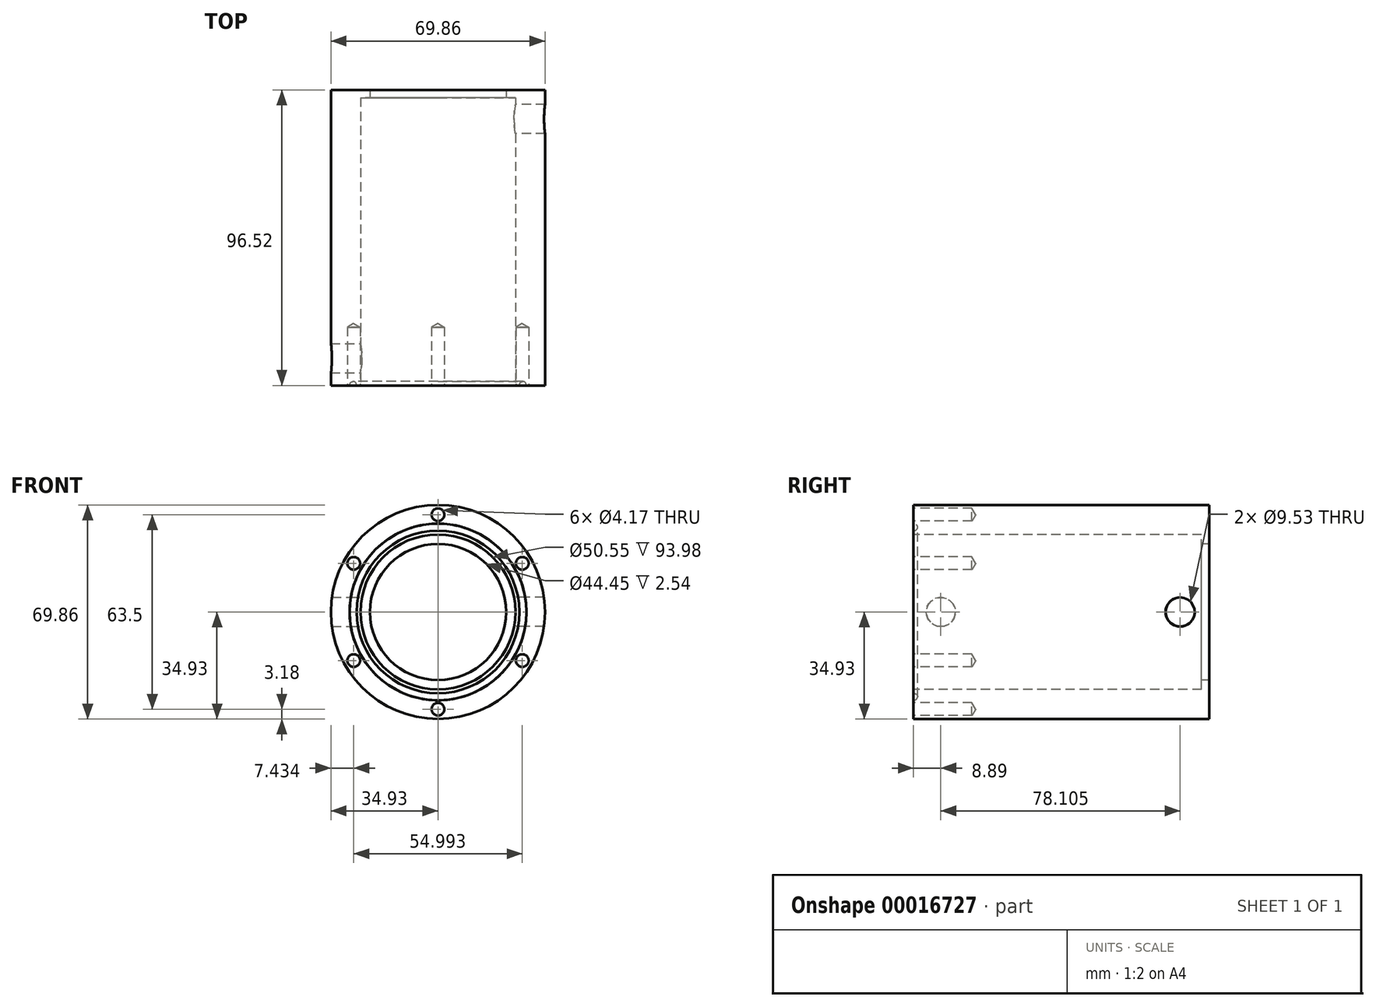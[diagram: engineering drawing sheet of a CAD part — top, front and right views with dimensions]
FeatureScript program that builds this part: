
annotation { "Feature Type Name" : "Feature", "Feature Type Description" : "" }
export const myFeature = defineFeature(function(context is Context, id is Id, definition is map)
    precondition{}
    {
        {
            var Q0;
            Q0=qCreatedBy(makeId("Front.planeOp"),FACE);
            var sketch = newSketch(context, id + "F0", { "sketchPlane" : qUnion([Q0])});
            skCircle(sketch, "E0", {"center": v(0, 0) * mm, "radius": 34.93 * mm});
            skSolve(sketch);
        }
        {
            var Q0;
            Q0=makeQuery(id+"F0.imprint","IMPRINT",FACE,{"disambiguationData":[TD([[makeQuery(id+"F0.imprint","IMPRINT",EDGE,{"derivedFrom":sQuery(id+"F0.wireOp",EDGE,"E0")}),1.0]])]});
            extrude(context, id + "F1", {"entities" : qUnion([Q0]), "oppositeDirection" : true, "depth" : 96.52 * mm});
        }
        {
            var Q0;
            Q0=qCreatedBy(makeId("Front.planeOp"),FACE);
            var sketch = newSketch(context, id + "F2", { "sketchPlane" : qUnion([Q0])});
            skPoint(sketch, "E1", {"position": v(0, 0) * mm});
            skSolve(sketch);
        }
        {
            var Q0;
            Q0=sQuery(id+"F2.wireOp",VERTEX,"E1");
            var Q1;
            Q1=makeQuery(id+"F1.opExtrude","SWEPT_BODY",BODY,{"disambiguationData":[OSD([sQuery(id+"F0.wireOp",EDGE,"E0")])]});
            hole(context, id + "F3", {"style" : HoleStyle.C_BORE, "holeDiameter" : 44.45 * mm, "cBoreDiameter" : 50.55 * mm, "cBoreDepth" : 93.98 * mm, "endStyle" : HoleEndStyle.THROUGH, "locations" : qUnion([Q0]), "scope" : qUnion([Q1])});
        }
        {
            var Q0;
            Q0=qCreatedBy(makeId("Front.planeOp"),FACE);
            var sketch = newSketch(context, id + "F4", { "sketchPlane" : qUnion([Q0])});
            skCircle(sketch, "E2", {"center": v(0, 0) * mm, "radius": 31.75 * mm});
            skPoint(sketch, "E3", {"position": v(0, 31.75) * mm});
            skPoint(sketch, "E4.1.0", {"position": v(-27.5, 15.88) * mm});
            skPoint(sketch, "E4.2.0", {"position": v(-27.5, -15.87) * mm});
            skPoint(sketch, "E4.3.0", {"position": v(0, -31.75) * mm});
            skPoint(sketch, "E4.4.0", {"position": v(27.5, -15.88) * mm});
            skPoint(sketch, "E5.0.5.0", {"position": v(27.5, 15.88) * mm});
            skSolve(sketch);
        }
        {
            var Q0;
            Q0=sQuery(id+"F4.wireOp",VERTEX,"E3");
            var Q1;
            Q1=sQuery(id+"F4.wireOp",VERTEX,"E4.4.0");
            var Q2;
            Q2=sQuery(id+"F4.wireOp",VERTEX,"E4.3.0");
            var Q3;
            Q3=sQuery(id+"F4.wireOp",VERTEX,"E4.2.0");
            var Q4;
            Q4=sQuery(id+"F4.wireOp",VERTEX,"E4.1.0");
            var Q5;
            Q5=sQuery(id+"F4.wireOp",VERTEX,"E5.0.5.0");
            var Q6;
            Q6=makeQuery(id+"F1.opExtrude","SWEPT_BODY",BODY,{"disambiguationData":[OSD([sQuery(id+"F0.wireOp",EDGE,"E0")])]});
            hole(context, id + "F5", {"style" : HoleStyle.SIMPLE, "holeDiameter" : 4.17 * mm, "endStyle" : HoleEndStyle.BLIND, "holeDepth" : 19.05 * mm, "locations" : qUnion([Q0, Q1, Q2, Q3, Q4, Q5]), "scope" : qUnion([Q6])});
        }
        {
            var Q0;
            Q0=qCreatedBy(makeId("Right.planeOp"),FACE);
            var sketch = newSketch(context, id + "F6", { "sketchPlane" : qUnion([Q0])});
            skEllipse(sketch, "E6", {"center": v(0, 27.69) * mm, "majorRadius": 1.14 * mm, "minorRadius": 1.33 * mm, "majorAxis": v(0, 1)});
            skSolve(sketch);
        }
        {
            var Q0;
            Q0=qCreatedBy(makeId("Right.planeOp"),FACE);
            var sketch = newSketch(context, id + "F7", { "sketchPlane" : qUnion([Q0])});
            skLineSegment(sketch, "E7", {"start": v(-93.1, 0) * mm, "end": v(96.45, 0) * mm});
            skSolve(sketch);
        }
        {
            var Q0;
            Q0=qCreatedBy(makeId("Right.planeOp"),FACE);
            var sketch = newSketch(context, id + "F8", { "sketchPlane" : qUnion([Q0])});
            skPoint(sketch, "E8", {"position": v(8.9, 0) * mm});
            skPoint(sketch, "E9", {"position": v(87, 0) * mm});
            skSolve(sketch);
        }
        {
            var Q0;
            Q0=sQuery(id+"F8.wireOp",VERTEX,"E8");
            var Q1;
            Q1=makeQuery(id+"F1.opExtrude","SWEPT_BODY",BODY,{"disambiguationData":[OSD([sQuery(id+"F0.wireOp",EDGE,"E0")])]});
            hole(context, id + "F9", {"style" : HoleStyle.SIMPLE, "holeDiameter" : 9.52 * mm, "endStyle" : HoleEndStyle.THROUGH, "locations" : qUnion([Q0]), "scope" : qUnion([Q1])});
        }
        {
            var Q0;
            Q0=sQuery(id+"F8.wireOp",VERTEX,"E9");
            var Q1;
            Q1=makeQuery(id+"F1.opExtrude","SWEPT_BODY",BODY,{"disambiguationData":[OSD([sQuery(id+"F0.wireOp",EDGE,"E0")])]});
            hole(context, id + "F10", {"style" : HoleStyle.SIMPLE, "holeDiameter" : 9.52 * mm, "endStyle" : HoleEndStyle.THROUGH, "oppositeDirection" : true, "locations" : qUnion([Q0]), "scope" : qUnion([Q1])});
        }
        {
            var Q0;
            Q0=makeQuery(id+"F6.imprint","IMPRINT",FACE,{"disambiguationData":[TD([[makeQuery(id+"F6.imprint","IMPRINT",EDGE,{"derivedFrom":sQuery(id+"F6.wireOp",EDGE,"E6")}),1.0]])]});
            var Q1;
            Q1=sQuery(id+"F7.wireOp",EDGE,"E7");
            revolve(context, id + "F11", {"operationType" : NewBodyOperationType.REMOVE, "entities" : qUnion([Q0]), "axis" : qUnion([Q1]), "revolveType" : RevolveType.FULL, "oppositeDirection" : true});
        }
    });
